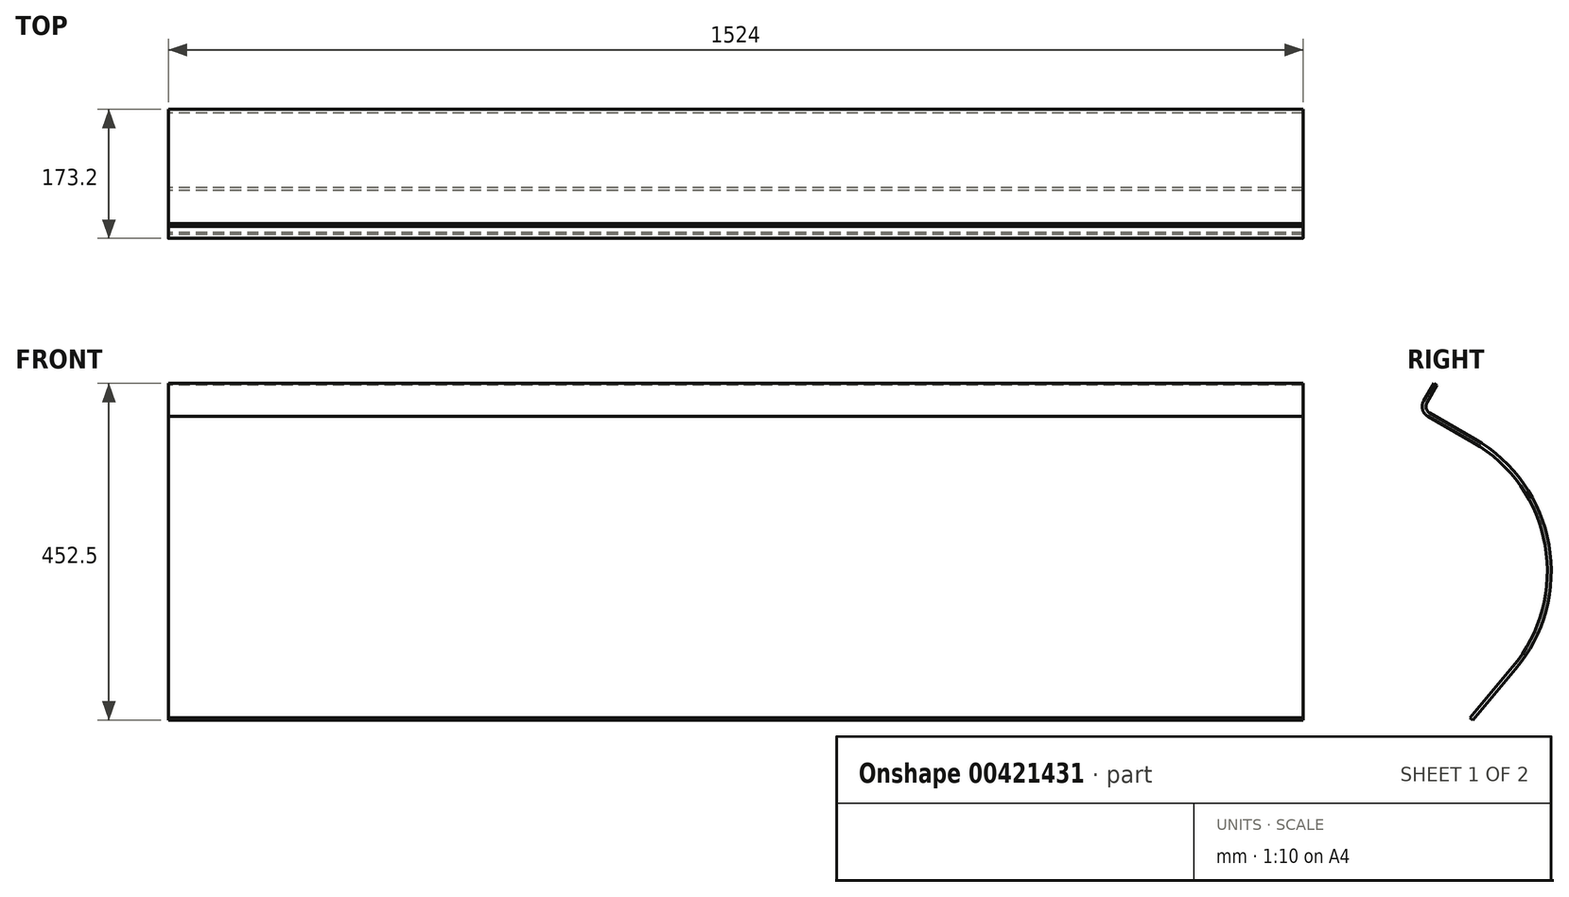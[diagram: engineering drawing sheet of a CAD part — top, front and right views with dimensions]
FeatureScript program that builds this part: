
annotation { "Feature Type Name" : "Feature", "Feature Type Description" : "" }
export const myFeature = defineFeature(function(context is Context, id is Id, definition is map)
    precondition{}
    {
        {
            var Q0;
            Q0=qCreatedBy(makeId("Right.planeOp"),FACE);
            var sketch = newSketch(context, id + "F0", { "sketchPlane" : qUnion([Q0])});
            skLineSegment(sketch, "E0", {"start": v(0, 0) * mm, "end": v(57.16, 68.12) * mm});
            skArc(sketch, "E1", {"start": v(57.16, 68.12) * mm, "mid": v(102.05, 235.63) * mm, "end": v(2.58, 377.68) * mm});
            skLineSegment(sketch, "E2", {"start": v(-100, 200) * mm, "end": v(73.2, 500) * mm, "construction": true});
            skLineSegment(sketch, "E3", {"start": v(2.58, 377.68) * mm, "end": v(-58.04, 412.68) * mm});
            skLineSegment(sketch, "E4", {"start": v(-61.7, 426.34) * mm, "end": v(-48.04, 450) * mm});
            skPoint(sketch, "E5.visualSharp", {"position": v(-66.7, 417.68) * mm});
            skArc(sketch, "E5.filletArc", {"start": v(-61.7, 426.34) * mm, "mid": v(-62.7, 418.75) * mm, "end": v(-58.04, 412.68) * mm});
            skLineSegment(sketch, "E6", {"start": v(0, 0) * mm, "end": v(-3.83, 3.21) * mm});
            skLineSegment(sketch, "E7", {"start": v(-48.04, 450) * mm, "end": v(-52.37, 452.5) * mm});
            skLineSegment(sketch, "E8", {"start": v(-52.37, 452.5) * mm, "end": v(-66.03, 428.84) * mm});
            skLineSegment(sketch, "E9", {"start": v(-60.4, 408.26) * mm, "end": v(0.08, 373.35) * mm});
            skArc(sketch, "E10", {"start": v(53.33, 71.34) * mm, "mid": v(97.12, 234.76) * mm, "end": v(0.08, 373.35) * mm});
            skLineSegment(sketch, "E11", {"start": v(-3.83, 3.21) * mm, "end": v(53.33, 71.34) * mm});
            skArc(sketch, "E12.trimOffspring", {"start": v(-66.03, 428.84) * mm, "mid": v(-67.5, 417.37) * mm, "end": v(-60.4, 408.26) * mm});
            skSolve(sketch);
        }
        {
            var Q0;
            Q0 = qSketchRegion(id + "F0", true);
            extrude(context, id + "F1", {"entities" : qUnion([Q0]), "depth" : 1524 * mm});
        }
    });
